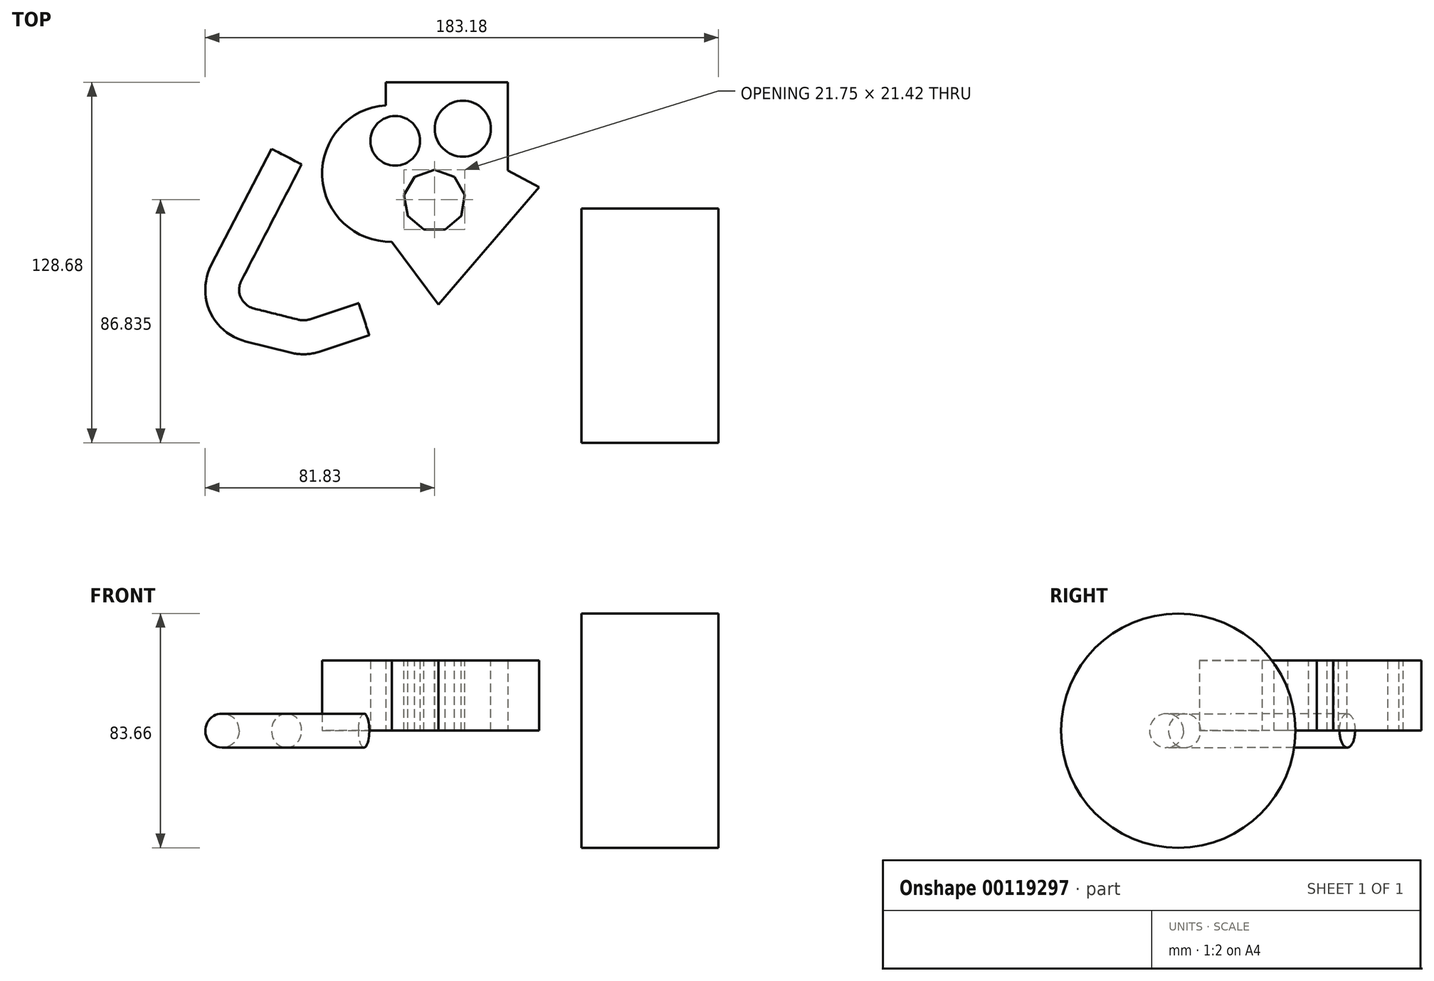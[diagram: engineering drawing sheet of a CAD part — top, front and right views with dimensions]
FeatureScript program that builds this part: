
annotation { "Feature Type Name" : "Feature", "Feature Type Description" : "" }
export const myFeature = defineFeature(function(context is Context, id is Id, definition is map)
    precondition{}
    {
        {
            var Q0;
            Q0=qCreatedBy(makeId("Top.planeOp"),FACE);
            var sketch = newSketch(context, id + "F0", { "sketchPlane" : qUnion([Q0])});
            skLineSegment(sketch, "E0", {"start": v(26.24, 28.25) * mm, "end": v(37.37, 22.4) * mm});
            skLineSegment(sketch, "E1", {"start": v(37.37, 22.4) * mm, "end": v(1.43, -19.54) * mm});
            skLineSegment(sketch, "E2", {"start": v(1.43, -19.54) * mm, "end": v(-15.2, 2.84) * mm});
            skArc(sketch, "E3", {"start": v(-17.4, 51.59) * mm, "mid": v(-40.07, 26.14) * mm, "end": v(-15.2, 2.84) * mm});
            skPoint(sketch, "E4.orphan", {"position": v(0, 42.07) * mm});
            skLineSegment(sketch, "E5.bottom", {"start": v(-17.4, 59.76) * mm, "end": v(26.24, 59.76) * mm});
            skLineSegment(sketch, "E5.left", {"start": v(-17.4, 59.76) * mm, "end": v(-17.4, 51.59) * mm});
            skLineSegment(sketch, "E5.right", {"start": v(26.24, 59.76) * mm, "end": v(26.24, 28.25) * mm});
            skCircle(sketch, "E6", {"center": v(-14, 38.89) * mm, "radius": 8.84 * mm});
            skSolve(sketch);
        }
        {
            var Q0;
            Q0=makeQuery(id+"F0.imprint","IMPRINT",FACE,{"disambiguationData":[TD([[makeQuery(id+"F0.imprint","IMPRINT",EDGE,{"derivedFrom":sQuery(id+"F0.wireOp",EDGE,"E0")}),-1.0]])]});
            extrude(context, id + "F1", {"entities" : qUnion([Q0]), "depth" : 25 * mm});
        }
        {
            var Q0;
            Q0=makeQuery(id+"F1.opExtrude","CAP_FACE",FACE,{"disambiguationData":[OSD([sQuery(id+"F0.wireOp",EDGE,"E0"),sQuery(id+"F0.wireOp",EDGE,"E1"),sQuery(id+"F0.wireOp",EDGE,"E2"),sQuery(id+"F0.wireOp",EDGE,"E3"),sQuery(id+"F0.wireOp",EDGE,"E5.bottom"),sQuery(id+"F0.wireOp",EDGE,"E5.left"),sQuery(id+"F0.wireOp",EDGE,"E5.right"),sQuery(id+"F0.wireOp",EDGE,"E6")])],"isStart":false});
            var sketch = newSketch(context, id + "F2", { "sketchPlane" : qUnion([Q0])});
            skCircle(sketch, "E7.cCircle", {"center": v(0, 17.58) * mm, "radius": 10.38 * mm, "construction": true});
            skLineSegment(sketch, "E7.0", {"start": v(3.78, 7.2) * mm, "end": v(-3.78, 7.2) * mm});
            skLineSegment(sketch, "E7.1", {"start": v(-3.78, 7.2) * mm, "end": v(-9.56, 12.06) * mm});
            skLineSegment(sketch, "E7.2", {"start": v(-9.56, 12.06) * mm, "end": v(-10.87, 19.5) * mm});
            skLineSegment(sketch, "E7.3", {"start": v(-10.87, 19.5) * mm, "end": v(-7.1, 26.04) * mm});
            skLineSegment(sketch, "E7.4", {"start": v(-7.1, 26.04) * mm, "end": v(0, 28.62) * mm});
            skLineSegment(sketch, "E7.5", {"start": v(0, 28.62) * mm, "end": v(7.1, 26.04) * mm});
            skLineSegment(sketch, "E7.6", {"start": v(7.1, 26.04) * mm, "end": v(10.87, 19.5) * mm});
            skLineSegment(sketch, "E7.7", {"start": v(10.87, 19.5) * mm, "end": v(9.56, 12.06) * mm});
            skLineSegment(sketch, "E7.8", {"start": v(9.56, 12.06) * mm, "end": v(3.78, 7.2) * mm});
            skPoint(sketch, "E7.0.midPoint", {"position": v(0, 7.2) * mm});
            skCircle(sketch, "E8.0", {"center": v(10.14, 43.22) * mm, "radius": 10 * mm});
            skSolve(sketch);
        }
        {
            var Q0;
            Q0 = qSketchRegion(id + "F2", true);
            extrude(context, id + "F3", {"entities" : qUnion([Q0]), "operationType" : NewBodyOperationType.REMOVE, "oppositeDirection" : true, "depth" : 25 * mm});
        }
        {
            var Q0;
            Q0=qCreatedBy(makeId("Top.planeOp"),FACE);
            var sketch = newSketch(context, id + "F4", { "sketchPlane" : qUnion([Q0])});
            skLineSegment(sketch, "E9.bottom", {"start": v(52.5, 14.74) * mm, "end": v(101.35, 14.74) * mm});
            skLineSegment(sketch, "E9.top", {"start": v(52.5, -27.1) * mm, "end": v(101.35, -27.1) * mm});
            skLineSegment(sketch, "E9.left", {"start": v(52.5, 14.74) * mm, "end": v(52.5, -27.1) * mm});
            skLineSegment(sketch, "E9.right", {"start": v(101.35, 14.74) * mm, "end": v(101.35, -27.1) * mm});
            skSolve(sketch);
        }
        {
            var Q0;
            Q0 = qSketchRegion(id + "F4", true);
            var Q1;
            Q1=sQuery(id+"F4.wireOp",EDGE,"E9.top");
            revolve(context, id + "F5", {"entities" : qUnion([Q0]), "axis" : qUnion([Q1]), "revolveType" : RevolveType.FULL});
        }
        {
            var Q0;
            Q0=qCreatedBy(makeId("Top.planeOp"),FACE);
            var sketch = newSketch(context, id + "F6", { "sketchPlane" : qUnion([Q0])});
            skLineSegment(sketch, "E10", {"start": v(-52.8, 33.27) * mm, "end": v(-74.32, -8.28) * mm});
            skLineSegment(sketch, "E11", {"start": v(-65.93, -26.87) * mm, "end": v(-49.9, -30.88) * mm});
            skLineSegment(sketch, "E12", {"start": v(-42.64, -30.6) * mm, "end": v(-25.18, -24.78) * mm});
            skPoint(sketch, "E13.visualSharp", {"position": v(-81.88, -22.88) * mm});
            skArc(sketch, "E13.filletArc", {"start": v(-74.32, -8.28) * mm, "mid": v(-74.62, -19.6) * mm, "end": v(-65.93, -26.87) * mm});
            skPoint(sketch, "E14.visualSharp", {"position": v(-46.23, -31.8) * mm});
            skArc(sketch, "E14.filletArc", {"start": v(-49.9, -30.88) * mm, "mid": v(-46.25, -31.25) * mm, "end": v(-42.64, -30.6) * mm});
            skSolve(sketch);
        }
        {
            var Q0;
            Q0=sQuery(id+"F6.wireOp",EDGE,"E10");
            var Q1;
            Q1=sQuery(id+"F6.wireOp",VERTEX,"E10.start");
            cPlane(context, id + "F7", {"entities" : qUnion([Q0, Q1]), "cplaneType" : CPlaneType.LINE_POINT, "offset" : 25 * mm, "width" : 150 * mm, "height" : 150 * mm});
        }
        {
            var Q0;
            Q0=qCreatedBy(id+"F7.planeOp",FACE);
            var sketch = newSketch(context, id + "F8", { "sketchPlane" : qUnion([Q0])});
            skPoint(sketch, "E15.0", {"position": v(-62.19, 0) * mm});
            skCircle(sketch, "E16", {"center": v(-62.19, 0) * mm, "radius": 6.06 * mm});
            skSolve(sketch);
        }
        {
            var Q0;
            Q0=makeQuery(id+"F8.imprint","IMPRINT",FACE,{"disambiguationData":[TD([[makeQuery(id+"F8.imprint","IMPRINT",EDGE,{"derivedFrom":sQuery(id+"F8.wireOp",EDGE,"E16")}),1.0]])]});
            var Q1;
            Q1=sQuery(id+"F8.wireOp",EDGE,"E16");
            var Q2;
            Q2=sQuery(id+"F6.wireOp",EDGE,"E10");
            var Q3;
            Q3=sQuery(id+"F6.wireOp",EDGE,"E13.filletArc");
            var Q4;
            Q4=sQuery(id+"F6.wireOp",EDGE,"E11");
            var Q5;
            Q5=sQuery(id+"F6.wireOp",EDGE,"E14.filletArc");
            var Q6;
            Q6=sQuery(id+"F6.wireOp",EDGE,"E12");
            sweep(context, id + "F9", {"profiles" : qUnion([Q0]), "surfaceProfiles" : qUnion([Q1]), "path" : qUnion([Q2, Q3, Q4, Q5, Q6])});
        }
        {
            var Q0;
            Q0 = qSketchRegion(id + "F8", true);
            extrude(context, id + "F10", {"entities" : qUnion([Q0]), "operationType" : NewBodyOperationType.ADD, "depth" : 25 * mm});
        }
    });
